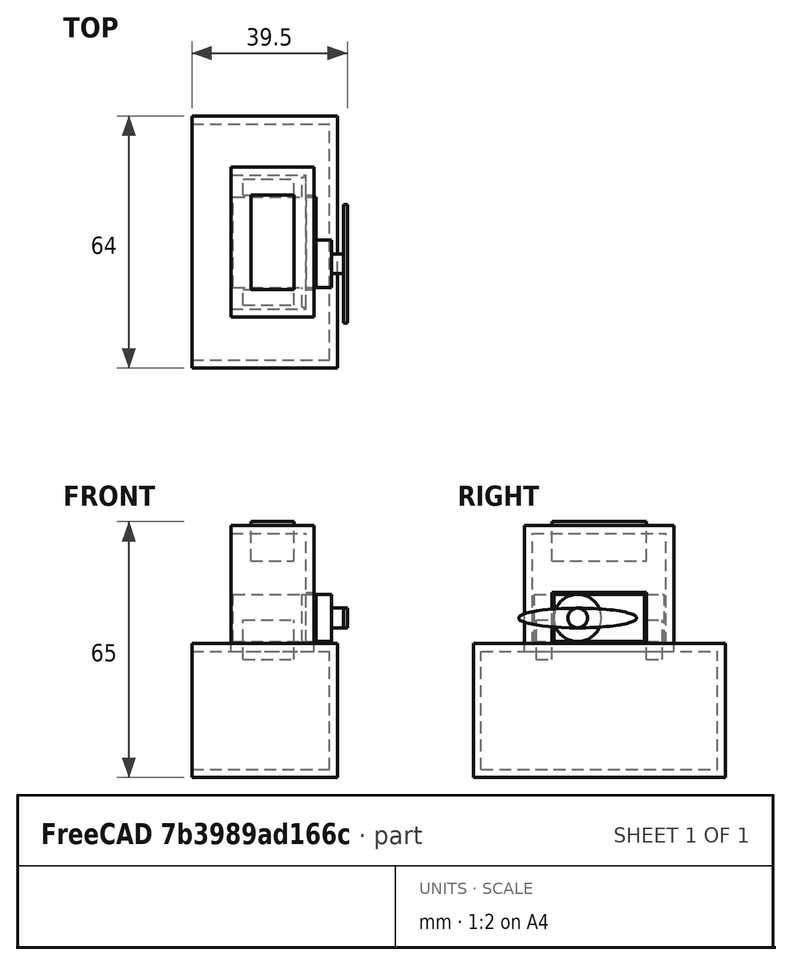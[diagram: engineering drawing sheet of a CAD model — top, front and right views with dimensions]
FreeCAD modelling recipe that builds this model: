
FCSTD DOCUMENT
Label: Servo
License: CC-BY 3.0
LicenseURL: http://creativecommons.org/licenses/by/3.0/
objects: Part::Box×10, Part::MultiFuse×4, Part::Cylinder×3, Part::Cut×2, Part::FeaturePython×1
note: 20 computed .brp shape members not serialized (recipe doc carries the construction recipe); baked Part::Feature solids carry a one-line shape summary decoded from their .brp

FEATURE [Part::Box] Box  label="ServoBody"
  Height = 21
  Length = 23
  Width = 12
FEATURE [Part::Cylinder] Cylinder  label="ServoBody2"
  Angle = 360
  Height = 4
  Placement = pos=(6,6,21) rot=(0,0,1;0rad)
  Radius = 6
FEATURE [Part::Box] Box001  label="ServoBody3"
  Height = 1
  Length = 33
  Placement = pos=(-5,0,17.5) rot=(0,0,1;0rad)
  Width = 12
FEATURE [Part::Cylinder] Cylinder001  label="ServoAxis"
  Angle = 360
  Height = 4
  Placement = pos=(6,6,24) rot=(0,0,1;0rad)
  Radius = 2.5
FEATURE [Part::MultiFuse] Fusion005  label="ServoArmL"
  Shapes = -> [Cylinder001,Box001,Box,Cylinder]
FEATURE [Part::Cylinder] Cylinder002
  Angle = 360
  Height = 2
  Radius = 2.5
FEATURE [Part::FeaturePython] Scale  # Draft clone (typed FeaturePython)
  Objects = -> [Cylinder002]
  Placement = pos=(0,0,1) rot=(0,0,1;0rad)
  Scale = (6,1,0.5)
FEATURE [Part::MultiFuse] Fusion  label="Arm"
  Placement = pos=(6,6,27) rot=(0,0,1;0rad)
  Shapes = -> [Cylinder002,Scale]
FEATURE [Part::MultiFuse] Fusion006  label="Servo"
  Placement = pos=(0.5,0.5,2.5) rot=(0.57735,0.57735,0.57735;2.0944rad)
  Shapes = -> [Fusion005,Fusion]
FEATURE [Part::Box] Box002
  Height = 28
  Length = 19
  Placement = pos=(0,-5,2) rot=(0,0,1;0rad)
  Width = 34
FEATURE [Part::Box] Box002001
  Height = 32
  Length = 21
  Placement = pos=(0,-7,0) rot=(0,0,1;0rad)
  Width = 38
FEATURE [Part::Box] Box002002
  Height = 13
  Length = 22
  Placement = pos=(0,0,2) rot=(0,0,1;0rad)
  Width = 24
FEATURE [Part::MultiFuse] Fusion007
  Shapes = -> [Box002,Box002002]
FEATURE [Part::Cut] Cut
  Base = -> Box002001
  Tool = -> Fusion007
FEATURE [Part::Box] Box002001002
  Height = 30
  Length = 35
  Placement = pos=(-10,-18,-30) rot=(0,0,1;0rad)
  Width = 60
FEATURE [Part::Box] Box002001003
  Height = 34
  Length = 37
  Placement = pos=(-10,-20,-32) rot=(0,0,1;0rad)
  Width = 64
FEATURE [Part::Cut] Cut001
  Base = -> Box002001003
  Tool = -> Box002001002
FEATURE [Part::Box] Box002001004
  Height = 10
  Length = 11
  Placement = pos=(5,0,23) rot=(0,0,1;0rad)
  Width = 24
FEATURE [Part::Box] Box002001005
  Height = 10
  Length = 13
  Placement = pos=(3,-4,-2) rot=(0,0,1;0rad)
  Width = 4
FEATURE [Part::Box] Box002001005001
  Height = 10
  Length = 13
  Placement = pos=(3,24,-2) rot=(0,0,1;0rad)
  Width = 4
